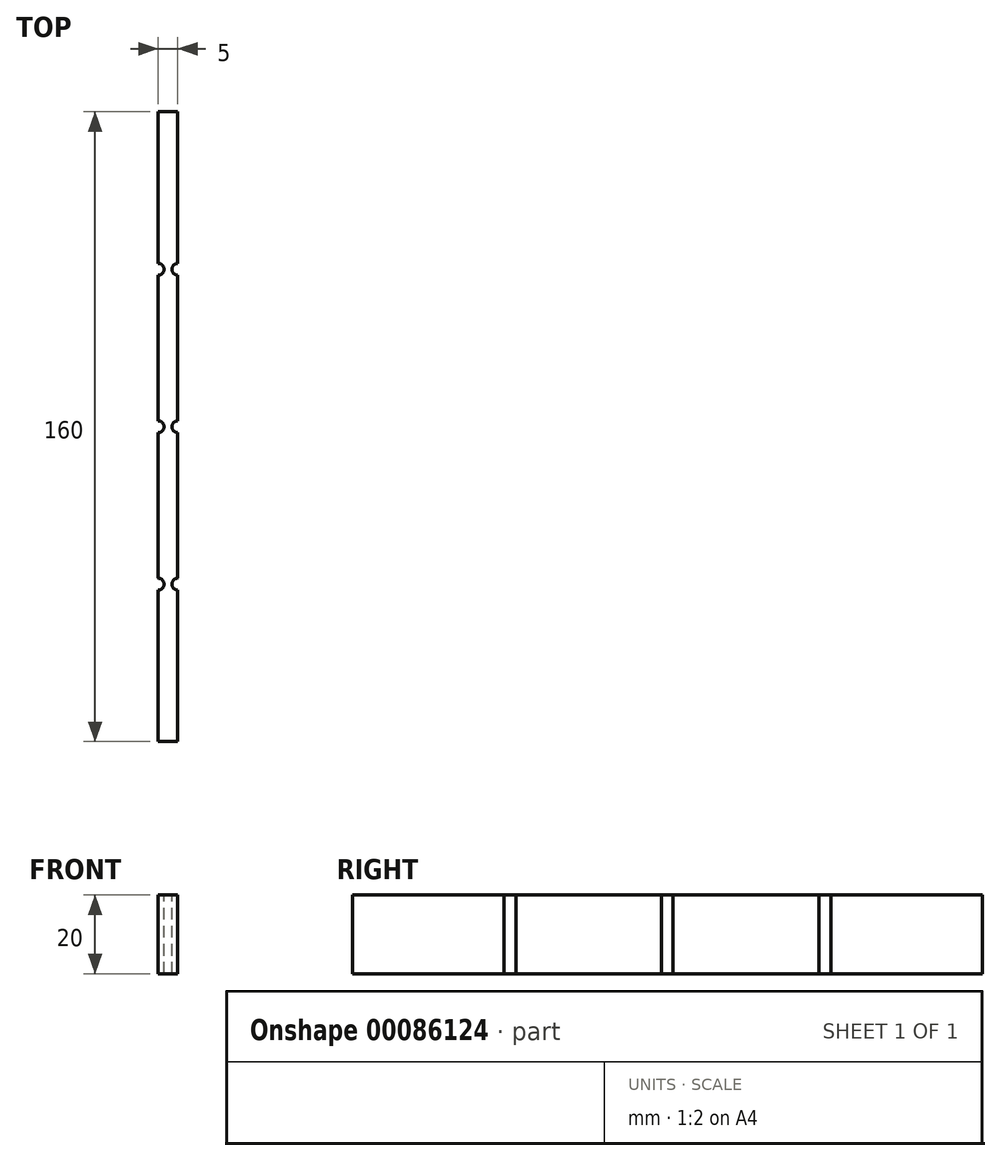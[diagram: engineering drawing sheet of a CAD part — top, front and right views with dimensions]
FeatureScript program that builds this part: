
annotation { "Feature Type Name" : "Feature", "Feature Type Description" : "" }
export const myFeature = defineFeature(function(context is Context, id is Id, definition is map)
    precondition{}
    {
        {
            var Q0;
            Q0=qCreatedBy(makeId("Top.planeOp"),FACE);
            var sketch = newSketch(context, id + "F0", { "sketchPlane" : qUnion([Q0])});
            skLineSegment(sketch, "E0.bottom", {"start": v(-10, 75) * mm, "end": v(-5, 75) * mm});
            skLineSegment(sketch, "E0.top", {"start": v(-10, -85) * mm, "end": v(-5, -85) * mm});
            skLineSegment(sketch, "E0.left", {"start": v(-10, 75) * mm, "end": v(-10, -85) * mm});
            skLineSegment(sketch, "E0.right", {"start": v(-5, 75) * mm, "end": v(-5, -85) * mm});
            skPoint(sketch, "E0.middle", {"position": v(-7.5, -5) * mm});
            skArc(sketch, "E1", {"start": v(-10, 33.5) * mm, "mid": v(-8.5, 35) * mm, "end": v(-10, 36.5) * mm});
            skArc(sketch, "E2", {"start": v(-5, 36.5) * mm, "mid": v(-6.5, 35) * mm, "end": v(-5, 33.5) * mm});
            skArc(sketch, "E3.MirrorCS", {"start": v(-10, -43.5) * mm, "mid": v(-8.5, -45) * mm, "end": v(-10, -46.5) * mm});
            skArc(sketch, "E4.MirrorCS", {"start": v(-5, -46.5) * mm, "mid": v(-6.5, -45) * mm, "end": v(-5, -43.5) * mm});
            skArc(sketch, "E5", {"start": v(-10, -6.5) * mm, "mid": v(-8.5, -5) * mm, "end": v(-10, -3.5) * mm});
            skArc(sketch, "E6.MirrorC", {"start": v(-5, -6.5) * mm, "mid": v(-6.5, -5) * mm, "end": v(-5, -3.5) * mm});
            skLineSegment(sketch, "E7", {"start": v(-10, -45) * mm, "end": v(-5, -45) * mm, "construction": true});
            skLineSegment(sketch, "E8", {"start": v(-10, -5) * mm, "end": v(-5, -5) * mm, "construction": true});
            skLineSegment(sketch, "E9", {"start": v(-10, 35) * mm, "end": v(-5, 35) * mm, "construction": true});
            skSolve(sketch);
        }
        {
            var Q0;
            {var subQ8=sQuery(id+"F0.wireOp",EDGE,"E0.bottom");Q0=makeQuery(id+"F0.imprint","IMPRINT",FACE,{"disambiguationData":[TD([[makeQuery(id+"F0.imprint","IMPRINT",EDGE,{"derivedFrom":subQ8}),-1.0]])]});}
            extrude(context, id + "F1", {"entities" : qUnion([Q0]), "oppositeDirection" : true, "depth" : 20 * mm});
        }
    });
